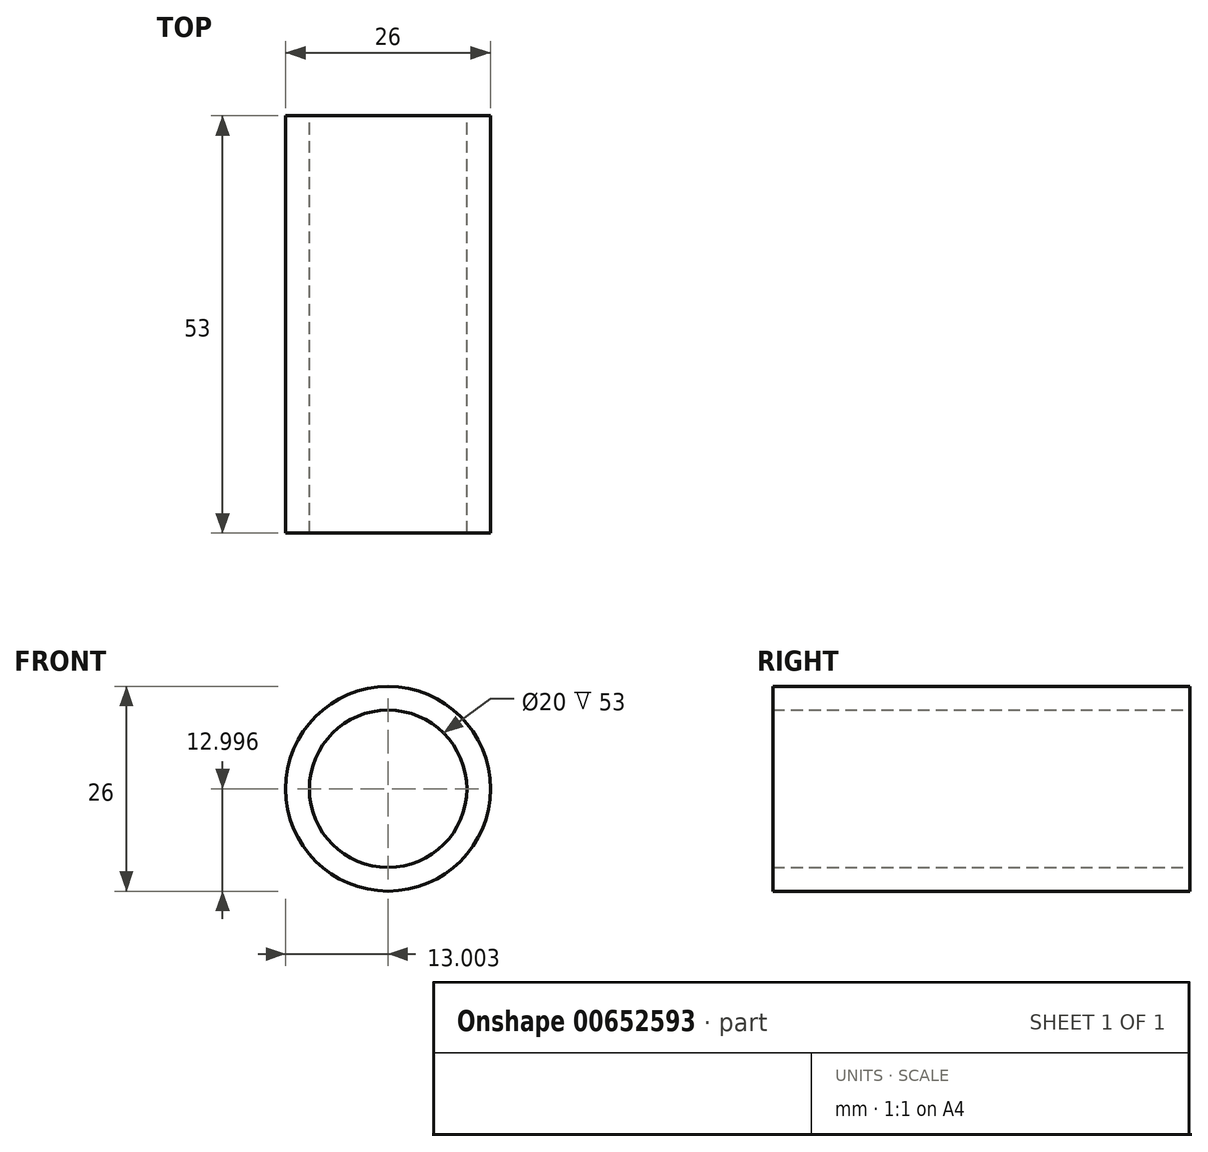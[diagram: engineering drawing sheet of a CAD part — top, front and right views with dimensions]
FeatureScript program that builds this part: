
annotation { "Feature Type Name" : "Feature", "Feature Type Description" : "" }
export const myFeature = defineFeature(function(context is Context, id is Id, definition is map)
    precondition{}
    {
        {
            var Q0;
            Q0=qCreatedBy(makeId("Front.planeOp"),FACE);
            var sketch = newSketch(context, id + "F0", { "sketchPlane" : qUnion([Q0])});
            skCircle(sketch, "E0", {"center": v(0.15, -0.61) * mm, "radius": 10 * mm});
            skCircle(sketch, "E1", {"center": v(0.15, -0.61) * mm, "radius": 13 * mm});
            skSolve(sketch);
        }
        {
            var Q0;
            Q0 = qSketchRegion(id + "F0", true);
            extrude(context, id + "F1", {"entities" : qUnion([Q0]), "depth" : (20 + 33) * mm, "offsetDistance" : 25 * mm});
        }
    });
